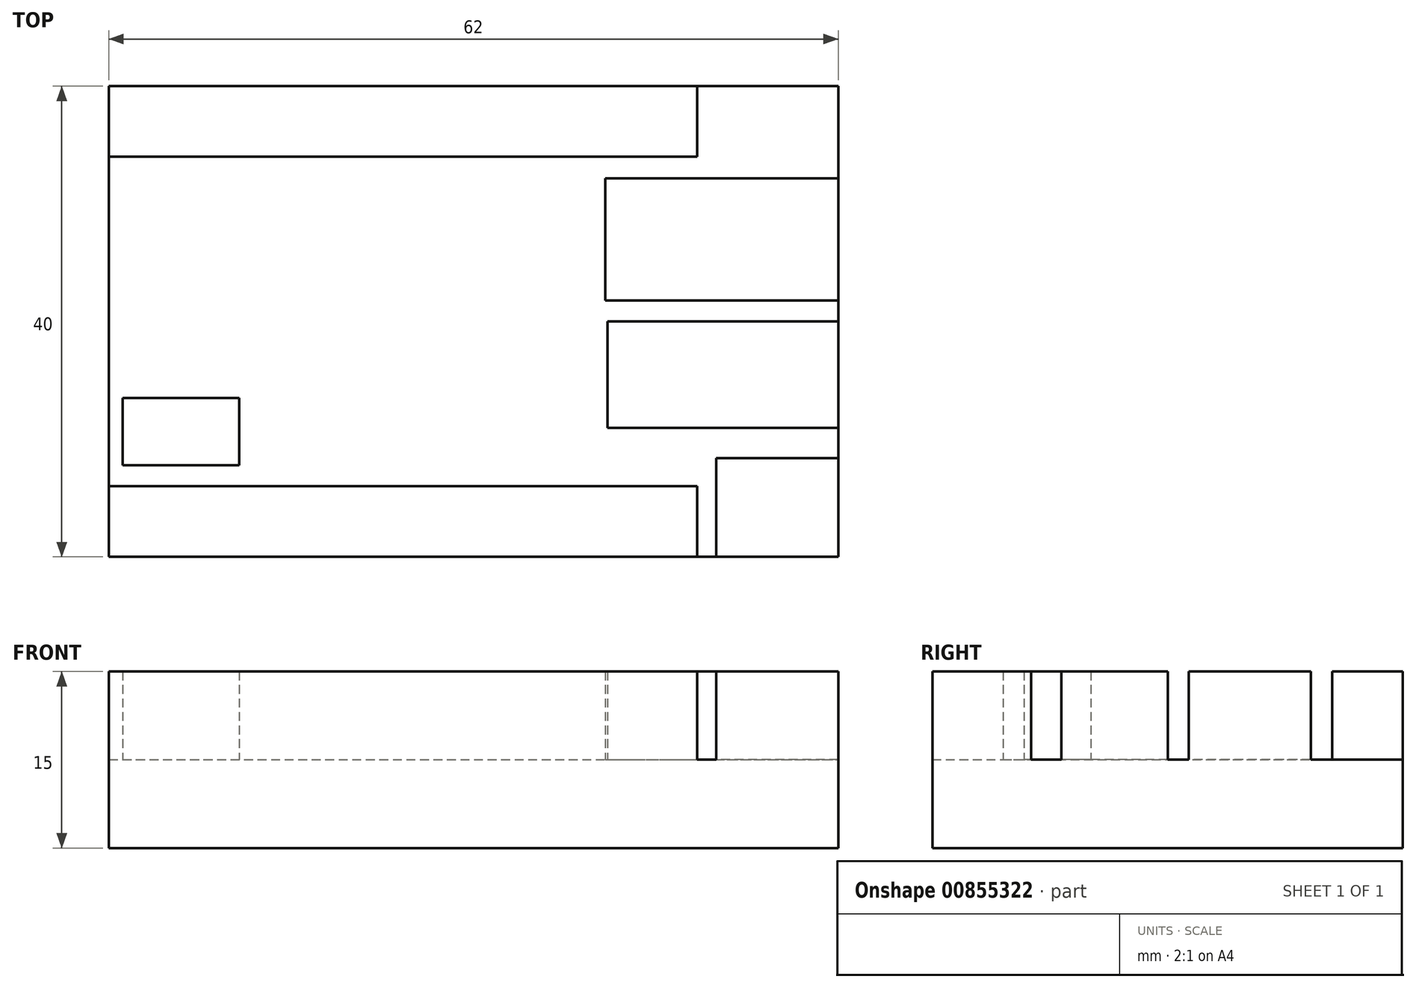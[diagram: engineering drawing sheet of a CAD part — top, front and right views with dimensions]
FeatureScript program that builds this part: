
annotation { "Feature Type Name" : "Feature", "Feature Type Description" : "" }
export const myFeature = defineFeature(function(context is Context, id is Id, definition is map)
    precondition{}
    {
        {
            var Q0;
            Q0=qCreatedBy(makeId("Top.planeOp"),FACE);
            var sketch = newSketch(context, id + "F0", { "sketchPlane" : qUnion([Q0])});
            skLineSegment(sketch, "E0.bottom", {"start": v(31, -20) * mm, "end": v(-31, -20) * mm});
            skLineSegment(sketch, "E0.top", {"start": v(31, 20) * mm, "end": v(-31, 20) * mm});
            skLineSegment(sketch, "E0.left", {"start": v(31, -20) * mm, "end": v(31, 20) * mm});
            skLineSegment(sketch, "E0.right", {"start": v(-31, -20) * mm, "end": v(-31, 20) * mm});
            skPoint(sketch, "E0.middle", {"position": v(0, 0) * mm});
            skSolve(sketch);
        }
        {
            var Q0;
            Q0=makeQuery(id+"F0.imprint","IMPRINT",FACE,{"disambiguationData":[TD([[makeQuery(id+"F0.imprint","IMPRINT",EDGE,{"derivedFrom":sQuery(id+"F0.wireOp",EDGE,"E0.bottom")}),-1.0]])]});
            extrude(context, id + "F1", {"entities" : qUnion([Q0]), "depth" : 7.5 * mm, "offsetDistance" : 25 * mm});
        }
        {
            var Q0;
            Q0=makeQuery(id+"F1.opExtrude","CAP_FACE",FACE,{"disambiguationData":[OSD([sQuery(id+"F0.wireOp",EDGE,"E0.bottom"),sQuery(id+"F0.wireOp",EDGE,"E0.top"),sQuery(id+"F0.wireOp",EDGE,"E0.left"),sQuery(id+"F0.wireOp",EDGE,"E0.right")])],"isStart":false});
            var sketch = newSketch(context, id + "F2", { "sketchPlane" : qUnion([Q0])});
            skLineSegment(sketch, "E1.bottom", {"start": v(-31, 20) * mm, "end": v(19, 20) * mm});
            skLineSegment(sketch, "E1.top", {"start": v(-31, 14) * mm, "end": v(19, 14) * mm});
            skLineSegment(sketch, "E1.left", {"start": v(-31, 20) * mm, "end": v(-31, 14) * mm});
            skLineSegment(sketch, "E1.right", {"start": v(19, 20) * mm, "end": v(19, 14) * mm});
            skLineSegment(sketch, "E2.bottom", {"start": v(-31, -20) * mm, "end": v(19, -20) * mm});
            skLineSegment(sketch, "E2.top", {"start": v(-31, -14) * mm, "end": v(19, -14) * mm});
            skLineSegment(sketch, "E2.left", {"start": v(-31, -20) * mm, "end": v(-31, -14) * mm});
            skLineSegment(sketch, "E2.right", {"start": v(19, -20) * mm, "end": v(19, -14) * mm});
            skPoint(sketch, "E3", {"position": v(25.16, 17) * mm});
            skPoint(sketch, "E3.positionSnap0", {"position": v(19, 17) * mm});
            skCircle(sketch, "E4", {"center": v(25.16, 17) * mm, "radius": 2.32 * mm});
            skLineSegment(sketch, "E5.bottom", {"start": v(11.2, 12.18) * mm, "end": v(31, 12.18) * mm});
            skLineSegment(sketch, "E5.top", {"start": v(11.2, 1.8) * mm, "end": v(31, 1.8) * mm});
            skLineSegment(sketch, "E5.left", {"start": v(11.2, 12.18) * mm, "end": v(11.2, 1.8) * mm});
            skLineSegment(sketch, "E5.right", {"start": v(31, 12.18) * mm, "end": v(31, 1.8) * mm});
            skLineSegment(sketch, "E6.bottom", {"start": v(11.38, 0) * mm, "end": v(31, 0) * mm});
            skLineSegment(sketch, "E6.top", {"start": v(11.38, -9.03) * mm, "end": v(31, -9.03) * mm});
            skLineSegment(sketch, "E6.left", {"start": v(11.38, 0) * mm, "end": v(11.38, -9.03) * mm});
            skLineSegment(sketch, "E6.right", {"start": v(31, 0) * mm, "end": v(31, -9.03) * mm});
            skLineSegment(sketch, "E7.bottom", {"start": v(31, -20) * mm, "end": v(20.62, -20) * mm});
            skLineSegment(sketch, "E7.top", {"start": v(31, -11.6) * mm, "end": v(20.62, -11.6) * mm});
            skLineSegment(sketch, "E7.left", {"start": v(31, -20) * mm, "end": v(31, -11.6) * mm});
            skLineSegment(sketch, "E7.right", {"start": v(20.62, -20) * mm, "end": v(20.62, -11.6) * mm});
            skLineSegment(sketch, "E8.bottom", {"start": v(-29.82, -6.52) * mm, "end": v(-19.92, -6.52) * mm});
            skLineSegment(sketch, "E8.top", {"start": v(-29.82, -12.22) * mm, "end": v(-19.92, -12.22) * mm});
            skLineSegment(sketch, "E8.left", {"start": v(-29.82, -6.52) * mm, "end": v(-29.82, -12.22) * mm});
            skLineSegment(sketch, "E8.right", {"start": v(-19.92, -6.52) * mm, "end": v(-19.92, -12.22) * mm});
            skSolve(sketch);
        }
        {
            var Q0;
            Q0=makeQuery(id+"F2.imprint","IMPRINT",FACE,{"disambiguationData":[TD([[makeQuery(id+"F2.imprint","IMPRINT",EDGE,{"derivedFrom":sQuery(id+"F2.wireOp",EDGE,"E1.bottom")}),1.0]])]});
            var Q1;
            Q1=makeQuery(id+"F2.imprint","IMPRINT",FACE,{"disambiguationData":[TD([[makeQuery(id+"F2.imprint","IMPRINT",EDGE,{"derivedFrom":sQuery(id+"F2.wireOp",EDGE,"E2.bottom")}),-1.0]])]});
            var Q2;
            Q2=makeQuery(id+"F2.imprint","IMPRINT",FACE,{"disambiguationData":[TD([[makeQuery(id+"F2.imprint","IMPRINT",EDGE,{"derivedFrom":sQuery(id+"F2.wireOp",EDGE,"E5.bottom")}),-1.0]])]});
            var Q3;
            Q3=makeQuery(id+"F2.imprint","IMPRINT",FACE,{"disambiguationData":[TD([[makeQuery(id+"F2.imprint","IMPRINT",EDGE,{"derivedFrom":sQuery(id+"F2.wireOp",EDGE,"E6.bottom")}),-1.0]])]});
            var Q4;
            Q4=makeQuery(id+"F2.imprint","IMPRINT",FACE,{"disambiguationData":[TD([[makeQuery(id+"F2.imprint","IMPRINT",EDGE,{"derivedFrom":sQuery(id+"F2.wireOp",EDGE,"E7.bottom")}),-1.0]])]});
            var Q5;
            Q5=makeQuery(id+"F2.imprint","IMPRINT",FACE,{"disambiguationData":[TD([[makeQuery(id+"F2.imprint","IMPRINT",EDGE,{"derivedFrom":sQuery(id+"F2.wireOp",EDGE,"E8.bottom")}),-1.0]])]});
            extrude(context, id + "F3", {"entities" : qUnion([Q0, Q1, Q2, Q3, Q4, Q5]), "operationType" : NewBodyOperationType.ADD, "depth" : 7.5 * mm, "offsetDistance" : 25 * mm});
        }
    });
